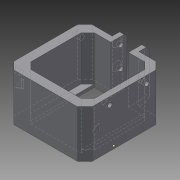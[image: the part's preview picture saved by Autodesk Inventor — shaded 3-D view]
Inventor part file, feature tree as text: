
AUTODESK INVENTOR PART (.ipt)
format: ipt  version: 2015 (Build 190159000, 159)  size: 226,304 bytes
history: native  units: mm
features: sketch x11, extrude x6, hole x4, chamfer x4
ambient origin geometry x8: Origin, YZ Plane, XZ Plane, XY Plane, X Axis, Y Axis, Z Axis, Center Point
bodies: Solid1 (feature_tree)
feature tree (25):
  extrude  "Extrusion1"  Depth=43.0mm
  hole  "Hole1"  [1 undecoded]
  chamfer  "Chamfer1"  Distance=30.0mm
  chamfer  "Chamfer2"  Distance=4.5mm Angle=45.0deg
  extrude  "Extrusion2"  Depth=2.0mm TaperAngle=0.0deg
  chamfer  "Chamfer3"  Distance=5.0mm Angle=45.0deg
  extrude  "Extrusion3"  Depth=7.5mm
  extrude  "Extrusion4"  Depth=1.0mm TaperAngle=0.0deg
  extrude  "Extrusion5"  Depth=3.0mm
  hole  "Hole2"  [1 undecoded]
  chamfer  "Chamfer4"  Distance=1.5mm
  hole  "Hole3"  [1 undecoded]
  extrude  "Extrusion6"  Depth=32.0mm TaperAngle=0.0deg
  sketch  "Sketch10"  dims[d30=10.0mm d31=0.0mm d32=1.0mm d33=0.0mm]
  hole  "Hole4"  [1 undecoded]
  sketch  "Sketch1"  dims[d0=43.0mm d1=43.0mm]
  sketch  "Sketch2"  dims[d2=6.0mm d3=4.0mm]
  sketch  "Sketch3"  dims[d4=6.0mm]
  sketch  "Sketch4"  dims[d5=4.0mm d6=30.0mm d7=0.0mm]
  sketch  "Sketch5"  dims[d8=5.0mm]
  sketch  "Sketch6"  dims[d9=41.0mm]
  sketch  "Sketch7"  dims[d10=3.0mm d11=6.0mm d12=4.0mm d13=2.0mm d14=90.0deg d15=5.0mm d16=20.594885mm d17=4.5mm d18=2.0mm d19=45.0deg]
  sketch  "Sketch8"  dims[d20=5.0mm d21=2.0mm d22=45.0deg d23=2.0mm d24=0.0mm d25=5.0mm d26=2.0mm d27=45.0deg]
  sketch  "Sketch9"  dims[d28=15.0mm d29=7.5mm]
  sketch  "Sketch11"  dims[d34=3.0mm d35=3.0mm d36=1.5mm d37=1.5mm d38=7.0mm d39=32.0mm d40=0.0mm d41=5.0mm d42=4.0mm d43=4.0mm d44=13.0mm d45=3.0mm d46=6.0mm d47=6.0mm d48=2.0mm d49=90.0deg d50=8.0mm d51=20.594885mm d52=2.0mm d53=2.0mm d54=45.0deg d55=3.0mm d56=6.0mm d57=6.0mm d58=2.0mm d59=90.0deg d60=8.0mm d61=20.594885mm d62=1.0mm d63=0.0mm d64=25.0mm d65=6.0mm d66=5.0mm d67=5.0mm d68=3.0mm d69=6.0mm d70=6.0mm d71=2.0mm d72=90.0deg d73=8.0mm d74=20.594885mm]
note: 4 required parameter values undecoded (feature->parameter linkage not recoverable at this tier; creation-order binding heuristic only, values carry confidence <= 0.55)
